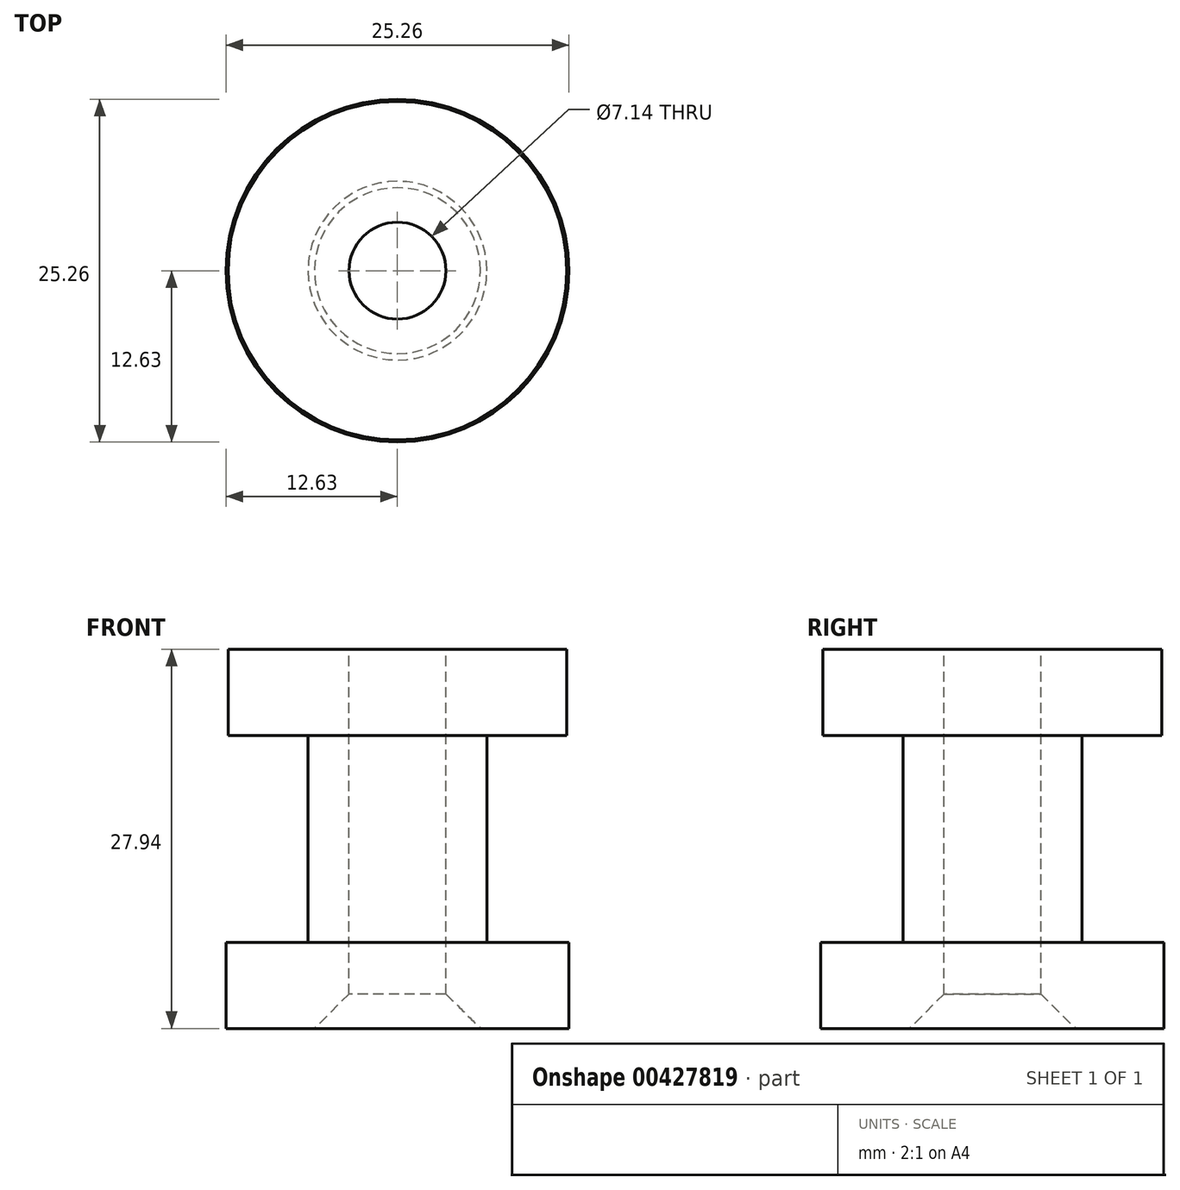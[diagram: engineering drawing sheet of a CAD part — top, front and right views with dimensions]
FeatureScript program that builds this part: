
annotation { "Feature Type Name" : "Feature", "Feature Type Description" : "" }
export const myFeature = defineFeature(function(context is Context, id is Id, definition is map)
    precondition{}
    {
        {
            var Q0;
            Q0=qCreatedBy(makeId("Top.planeOp"),FACE);
            var sketch = newSketch(context, id + "F0", { "sketchPlane" : qUnion([Q0])});
            skCircle(sketch, "E0", {"center": v(0, 0) * mm, "radius": 12.63 * mm});
            skSolve(sketch);
        }
        {
            var Q0;
            Q0 = qSketchRegion(id + "F0", true);
            extrude(context, id + "F1", {"entities" : qUnion([Q0]), "depth" : 6.35 * mm});
        }
        {
            var Q0;
            Q0=makeQuery(id+"F1.opExtrude","CAP_FACE",FACE,{"disambiguationData":[OSD([sQuery(id+"F0.wireOp",EDGE,"E0")])],"isStart":false});
            var sketch = newSketch(context, id + "F2", { "sketchPlane" : qUnion([Q0])});
            skCircle(sketch, "E1", {"center": v(0, 0) * mm, "radius": 6.58 * mm});
            skSolve(sketch);
        }
        {
            var Q0;
            Q0 = qSketchRegion(id + "F2", true);
            extrude(context, id + "F3", {"entities" : qUnion([Q0]), "operationType" : NewBodyOperationType.ADD, "depth" : 15.24 * mm});
        }
        {
            var Q0;
            Q0=makeQuery(id+"F3.opExtrude","CAP_FACE",FACE,{"disambiguationData":[OSD([sQuery(id+"F2.wireOp",EDGE,"E1")])],"isStart":false});
            var sketch = newSketch(context, id + "F4", { "sketchPlane" : qUnion([Q0])});
            skCircle(sketch, "E2", {"center": v(0, 0) * mm, "radius": 12.48 * mm});
            skSolve(sketch);
        }
        {
            var Q0;
            Q0 = qSketchRegion(id + "F4", true);
            extrude(context, id + "F5", {"entities" : qUnion([Q0]), "operationType" : NewBodyOperationType.ADD, "depth" : 6.35 * mm});
        }
        {
            var Q0;
            Q0=makeQuery(id+"F5.opExtrude","CAP_FACE",FACE,{"disambiguationData":[OSD([sQuery(id+"F4.wireOp",EDGE,"E2")])],"isStart":false});
            var sketch = newSketch(context, id + "F6", { "sketchPlane" : qUnion([Q0])});
            skCircle(sketch, "E3", {"center": v(0, 0) * mm, "radius": 3.57 * mm});
            skSolve(sketch);
        }
        {
            var Q0;
            Q0 = qSketchRegion(id + "F6", true);
            extrude(context, id + "F7", {"entities" : qUnion([Q0]), "operationType" : NewBodyOperationType.REMOVE, "endBound" : BoundingType.THROUGH_ALL, "oppositeDirection" : true, "depth" : 25.4 * mm});
        }
        {
            var Q0;
            Q0=makeQuery(id+"F7.boolean.opBoolean","COPY",EDGE,{"derivedFrom":makeQuery(id+"F7.opExtrude","CAP_EDGE",EDGE,{"disambiguationData":[OSD([sQuery(id+"F6.wireOp",EDGE,"E3")])],"isStart":true})});
            var Q1;
            Q1=makeQuery(id+"F7.boolean.opBoolean","INTERSECT",EDGE,{"derivedFrom":[makeQuery(id+"F1.opExtrude","CAP_FACE",FACE,{"disambiguationData":[OSD([sQuery(id+"F0.wireOp",EDGE,"E0")])],"isStart":true}),makeQuery(id+"F7.opExtrude","SWEPT_FACE",FACE,{"disambiguationData":[OSD([sQuery(id+"F6.wireOp",EDGE,"E3")])]})]});
            chamfer(context, id + "F8", {"entities" : qUnion([Q0, Q1]), "width" : 2.54 * mm, "tangentPropagation" : true});
        }
    });
